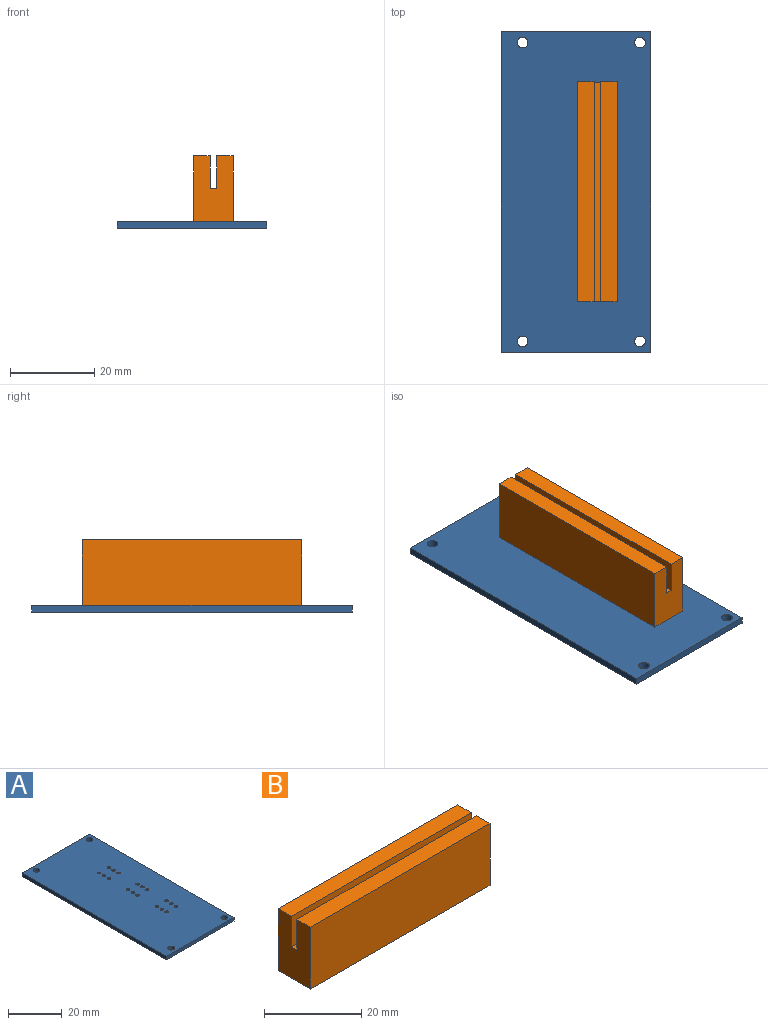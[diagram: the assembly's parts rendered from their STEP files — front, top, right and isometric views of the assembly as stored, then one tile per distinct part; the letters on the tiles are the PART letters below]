
ASSEMBLY  parts=2 mates=1
PART A: 28 faces, bbox 35.6x76.2x1.6 mm
  f0: plane 35.56x1.6mm, normal (0,-1,0), area 56.9mm2, adj f1,f25,f26,f27
  f1: plane 76.2x1.6mm, normal (1,0,0), area 121.9mm2, adj f0,f2,f26,f27
  f2: plane 35.56x1.6mm, normal (0,1,0), area 56.9mm2, adj f1,f25,f26,f27
  f3: cylinder r=0.64mm len=1.6mm, axis (0,0,-1), area 6.4mm2, adj f26,f27
  f4: cylinder r=0.64mm len=1.6mm, axis (0,0,-1), area 6.4mm2, adj f26,f27
  f5: cylinder r=0.64mm len=1.6mm, axis (0,0,-1), area 6.4mm2, adj f26,f27
  f6: cylinder r=0.64mm len=1.6mm, axis (0,0,-1), area 6.4mm2, adj f26,f27
  f7: cylinder r=0.64mm len=1.6mm, axis (0,0,-1), area 6.4mm2, adj f26,f27
  f8: cylinder r=0.64mm len=1.6mm, axis (0,0,-1), area 6.4mm2, adj f26,f27
  f9: cylinder r=0.64mm len=1.6mm, axis (0,0,-1), area 6.4mm2, adj f26,f27
  f10: cylinder r=0.64mm len=1.6mm, axis (0,0,-1), area 6.4mm2, adj f26,f27
  f11: cylinder r=0.64mm len=1.6mm, axis (0,0,-1), area 6.4mm2, adj f26,f27
  f12: cylinder r=0.64mm len=1.6mm, axis (0,0,-1), area 6.4mm2, adj f26,f27
  f13: cylinder r=0.64mm len=1.6mm, axis (0,0,-1), area 6.4mm2, adj f26,f27
  f14: cylinder r=0.64mm len=1.6mm, axis (0,0,-1), area 6.4mm2, adj f26,f27
  f15: cylinder r=1.27mm len=2.54mm, axis (0,0,-1), area 12.8mm2, adj f26,f27
  f16: cylinder r=1.27mm len=2.54mm, axis (0,0,-1), area 12.8mm2, adj f26,f27
  f17: cylinder r=1.27mm len=2.54mm, axis (0,0,-1), area 12.8mm2, adj f26,f27
  f18: cylinder r=1.27mm len=2.54mm, axis (0,0,-1), area 12.8mm2, adj f26,f27
  f19: cylinder r=0.64mm len=1.6mm, axis (0,0,-1), area 6.4mm2, adj f26,f27
  f20: cylinder r=0.64mm len=1.6mm, axis (0,0,-1), area 6.4mm2, adj f26,f27
  f21: cylinder r=0.64mm len=1.6mm, axis (0,0,-1), area 6.4mm2, adj f26,f27
  f22: cylinder r=0.64mm len=1.6mm, axis (0,0,-1), area 6.4mm2, adj f26,f27
  f23: cylinder r=0.64mm len=1.6mm, axis (0,0,-1), area 6.4mm2, adj f26,f27
  f24: cylinder r=0.64mm len=1.6mm, axis (0,0,-1), area 6.4mm2, adj f26,f27
  f25: plane 76.2x1.6mm, normal (-1,0,0), area 121.9mm2, adj f0,f2,f26,f27
  f26: plane 76.2x35.56mm, normal (0,0,1), area 2666.6mm2, adj f0,f1,f2,f3,f4,f5,f6,f7
  f27: plane 76.2x35.56mm, normal (0,0,-1), area 2666.6mm2, adj f0,f1,f2,f3,f4,f5,f6,f7
PART B: 10 faces, bbox 52.3x9.4x15.6 mm
  f0: plane 52.32x3.92mm, normal (0,0,1), area 205.3mm2, adj f1,f2,f3,f7
  f1: plane 15.6x9.4mm, normal (1,0,0), area 134.7mm2, adj f0,f2,f4,f5,f6,f7,f8,f9
  f2: plane 52.32x15.6mm, normal (0,1,0), area 816.3mm2, adj f0,f1,f3,f6
  f3: plane 15.6x9.4mm, normal (-1,0,0), area 134.7mm2, adj f0,f2,f4,f5,f6,f7,f8,f9
  f4: plane 52.32x15.6mm, normal (0,-1,0), area 816.3mm2, adj f1,f3,f5,f6
  f5: plane 52.32x3.92mm, normal (0,0,1), area 205.3mm2, adj f1,f3,f4,f8
  f6: plane 52.32x9.4mm, normal (0,0,-1), area 491.7mm2, adj f1,f2,f3,f4
  f7: plane 52.32x7.7mm, normal (0,-1,0), area 402.9mm2, adj f0,f1,f3,f9
  f8: plane 52.32x7.7mm, normal (0,1,0), area 402.9mm2, adj f1,f3,f5,f9
  f9: plane 52.32x1.55mm, normal (0,0,1), area 81.1mm2, adj f1,f3,f7,f8
PLACE A t=(53.73,30.54,-0.8)mm
PLACE B rot(axis=(0,0,-1),90deg) t=(36.33,42.48,0.8)mm
MATE fastened B.f6 <-> A.f26  axis (0,0,-1) through (41.03,68.64,0.8)mm
